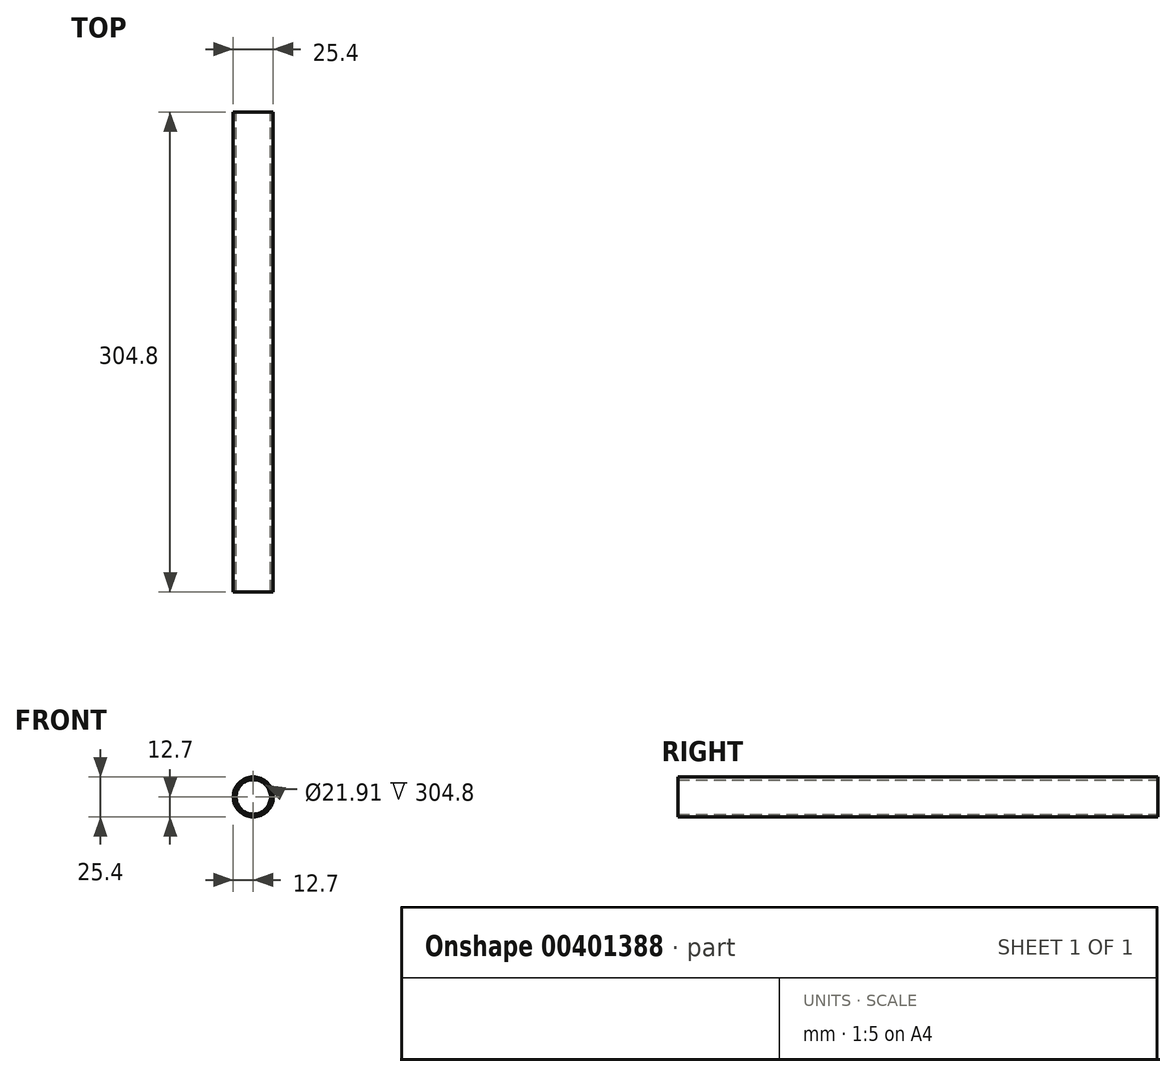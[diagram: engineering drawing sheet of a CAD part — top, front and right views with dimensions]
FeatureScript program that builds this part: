
annotation { "Feature Type Name" : "Feature", "Feature Type Description" : "" }
export const myFeature = defineFeature(function(context is Context, id is Id, definition is map)
    precondition{}
    {
        {
            var Q0;
            Q0=qCreatedBy(makeId("Front.planeOp"),FACE);
            var sketch = newSketch(context, id + "F0", { "sketchPlane" : qUnion([Q0])});
            skCircle(sketch, "E0", {"center": v(0, 0) * mm, "radius": 12.7 * mm});
            skCircle(sketch, "E1", {"center": v(0, 0) * mm, "radius": 10.95 * mm});
            skSolve(sketch);
        }
        {
            var Q0;
            Q0 = qSketchRegion(id + "F0", true);
            extrude(context, id + "F1", {"entities" : qUnion([Q0]), "depth" : 304.8 * mm});
        }
    });
